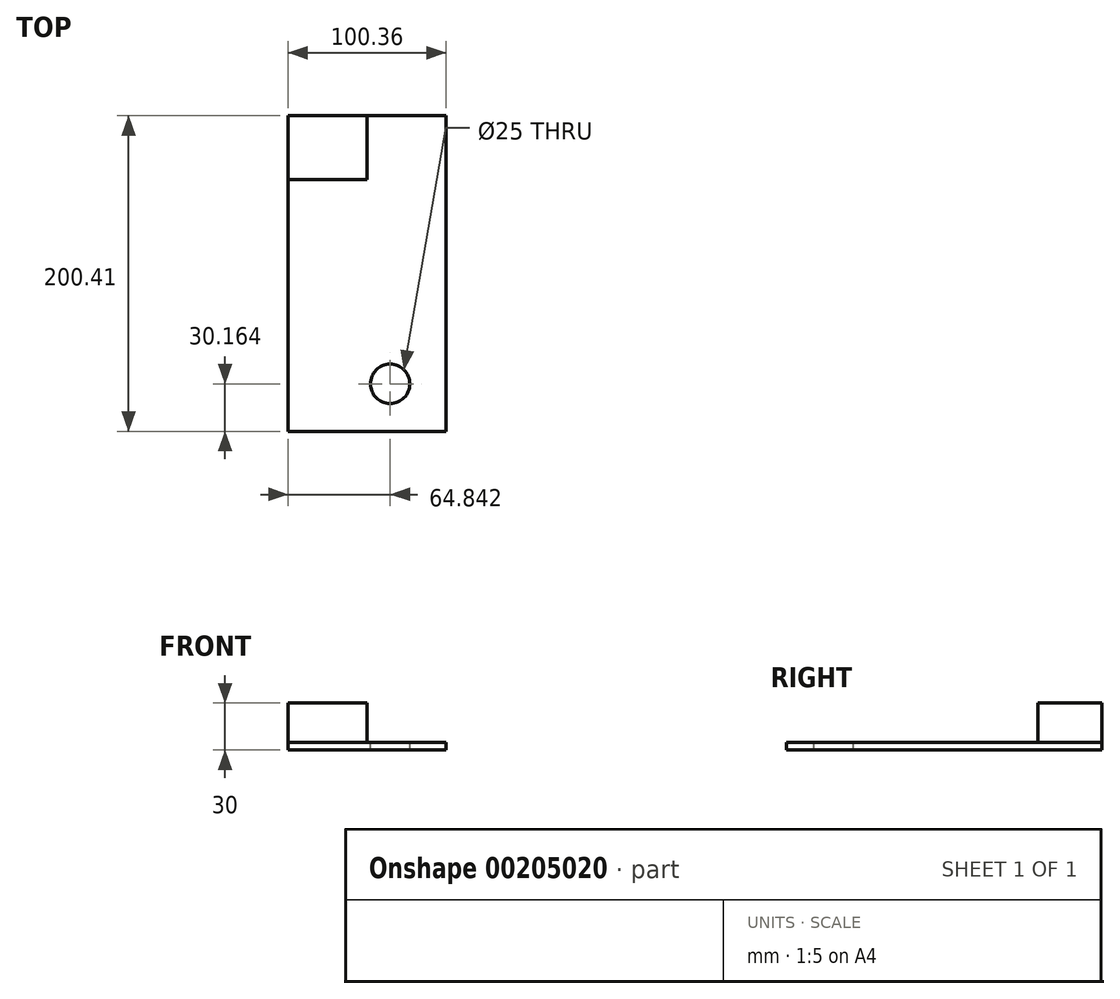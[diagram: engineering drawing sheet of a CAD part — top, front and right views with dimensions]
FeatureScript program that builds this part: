
annotation { "Feature Type Name" : "Feature", "Feature Type Description" : "" }
export const myFeature = defineFeature(function(context is Context, id is Id, definition is map)
    precondition{}
    {
        {
            var Q0;
            Q0=qCreatedBy(makeId("Top.planeOp"),FACE);
            var sketch = newSketch(context, id + "F0", { "sketchPlane" : qUnion([Q0])});
            skLineSegment(sketch, "E0.bottom", {"start": v(-76.8, 76.1) * mm, "end": v(23.57, 76.1) * mm});
            skLineSegment(sketch, "E0.top", {"start": v(-76.8, -124.32) * mm, "end": v(23.57, -124.32) * mm});
            skLineSegment(sketch, "E0.left", {"start": v(-76.8, 76.1) * mm, "end": v(-76.8, -124.32) * mm});
            skLineSegment(sketch, "E0.right", {"start": v(23.57, 76.1) * mm, "end": v(23.57, -124.32) * mm});
            skSolve(sketch);
        }
        {
            var Q0;
            Q0 = qSketchRegion(id + "F0", true);
            extrude(context, id + "F1", {"entities" : qUnion([Q0]), "depth" : 5 * mm});
        }
        {
            var Q0;
            Q0=makeQuery(id+"F1.opExtrude","CAP_FACE",FACE,{"disambiguationData":[OSD([sQuery(id+"F0.wireOp",EDGE,"E0.bottom"),sQuery(id+"F0.wireOp",EDGE,"E0.top"),sQuery(id+"F0.wireOp",EDGE,"E0.left"),sQuery(id+"F0.wireOp",EDGE,"E0.right")])],"isStart":false});
            var sketch = newSketch(context, id + "F2", { "sketchPlane" : qUnion([Q0])});
            skLineSegment(sketch, "E1.bottom", {"start": v(-76.8, 76.1) * mm, "end": v(-26.6, 76.1) * mm});
            skLineSegment(sketch, "E1.top", {"start": v(-76.8, 35.65) * mm, "end": v(-26.6, 35.65) * mm});
            skLineSegment(sketch, "E1.left", {"start": v(-76.8, 76.1) * mm, "end": v(-76.8, 35.65) * mm});
            skLineSegment(sketch, "E1.right", {"start": v(-26.6, 76.1) * mm, "end": v(-26.6, 35.65) * mm});
            skSolve(sketch);
        }
        {
            var Q0;
            Q0 = qSketchRegion(id + "F2", true);
            extrude(context, id + "F3", {"entities" : qUnion([Q0]), "operationType" : NewBodyOperationType.ADD, "depth" : 25 * mm});
        }
        {
            var Q0;
            Q0=makeQuery(id+"F1.opExtrude","CAP_FACE",FACE,{"disambiguationData":[OSD([sQuery(id+"F0.wireOp",EDGE,"E0.bottom"),sQuery(id+"F0.wireOp",EDGE,"E0.top"),sQuery(id+"F0.wireOp",EDGE,"E0.left"),sQuery(id+"F0.wireOp",EDGE,"E0.right")])],"isStart":false});
            var sketch = newSketch(context, id + "F4", { "sketchPlane" : qUnion([Q0])});
            skLineSegment(sketch, "E2.bottom", {"start": v(23.57, -124.32) * mm, "end": v(-11.95, -124.32) * mm});
            skLineSegment(sketch, "E2.top", {"start": v(23.57, -94.16) * mm, "end": v(-11.95, -94.16) * mm});
            skLineSegment(sketch, "E2.left", {"start": v(23.57, -124.32) * mm, "end": v(23.57, -94.16) * mm});
            skLineSegment(sketch, "E2.right", {"start": v(-11.95, -124.32) * mm, "end": v(-11.95, -94.16) * mm});
            skSolve(sketch);
        }
        {
            var Q0;
            Q0=sQuery(id+"F4.wireOp",VERTEX,"E2.top.end");
            var Q1;
            Q1=makeQuery(id+"F1.opExtrude","SWEPT_BODY",BODY,{"disambiguationData":[OSD([sQuery(id+"F0.wireOp",EDGE,"E0.bottom"),sQuery(id+"F0.wireOp",EDGE,"E0.top"),sQuery(id+"F0.wireOp",EDGE,"E0.left"),sQuery(id+"F0.wireOp",EDGE,"E0.right")])]});
            hole(context, id + "F5", {"style" : HoleStyle.SIMPLE, "endStyle" : HoleEndStyle.THROUGH, "holeDiameter" : 25 * mm, "locations" : qUnion([Q0]), "scope" : qUnion([Q1]), "isTappedThrough" : true});
        }
    });
